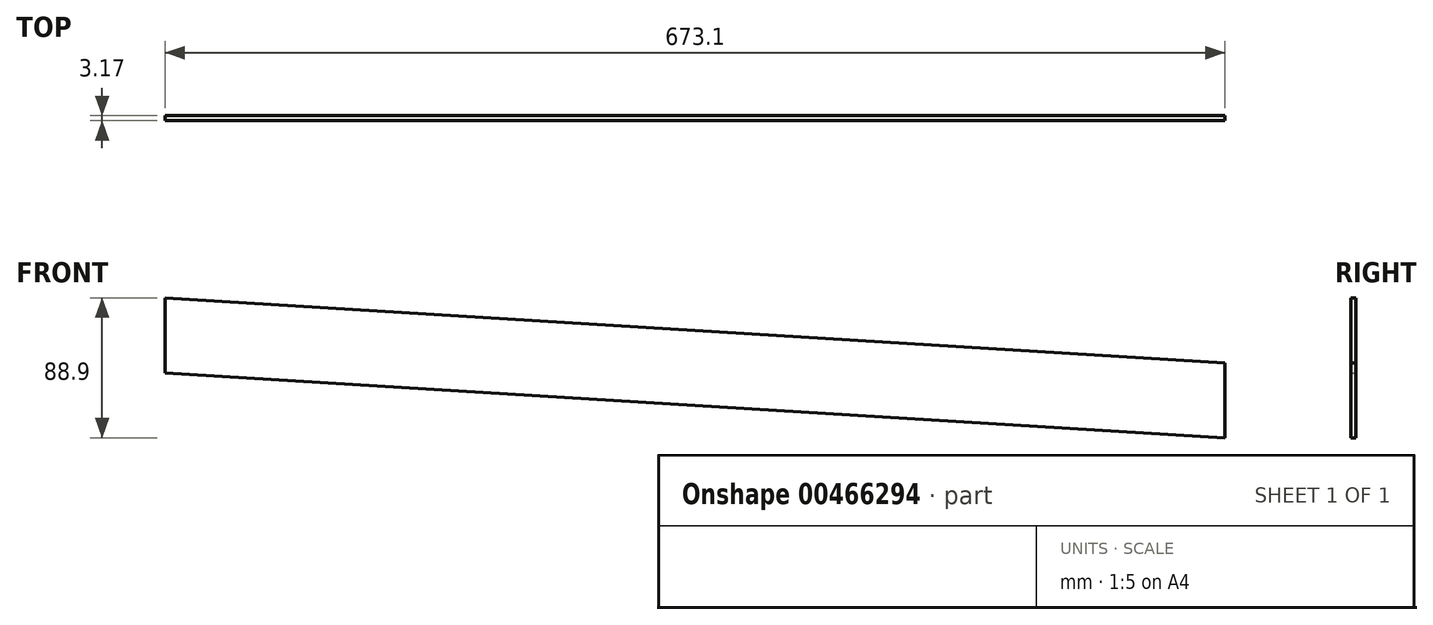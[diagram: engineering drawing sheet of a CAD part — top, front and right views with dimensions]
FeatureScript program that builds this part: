
annotation { "Feature Type Name" : "Feature", "Feature Type Description" : "" }
export const myFeature = defineFeature(function(context is Context, id is Id, definition is map)
    precondition{}
    {
        {
            var Q0;
            Q0=qCreatedBy(makeId("Front.planeOp"),FACE);
            var sketch = newSketch(context, id + "F0", { "sketchPlane" : qUnion([Q0])});
            skLineSegment(sketch, "E0", {"start": v(-202.24, -7.74) * mm, "end": v(-202.24, 39.89) * mm});
            skLineSegment(sketch, "E1", {"start": v(470.86, -1.39) * mm, "end": v(470.86, -49.01) * mm});
            skLineSegment(sketch, "E2", {"start": v(470.86, -49.01) * mm, "end": v(-202.24, -7.74) * mm});
            skLineSegment(sketch, "E3", {"start": v(-202.24, 39.89) * mm, "end": v(470.86, -1.39) * mm});
            skSolve(sketch);
        }
        {
            var Q0;
            Q0 = qSketchRegion(id + "F0", true);
            extrude(context, id + "F1", {"entities" : qUnion([Q0]), "depth" : 3.17 * mm, "offsetDistance" : 25.4 * mm});
        }
    });
